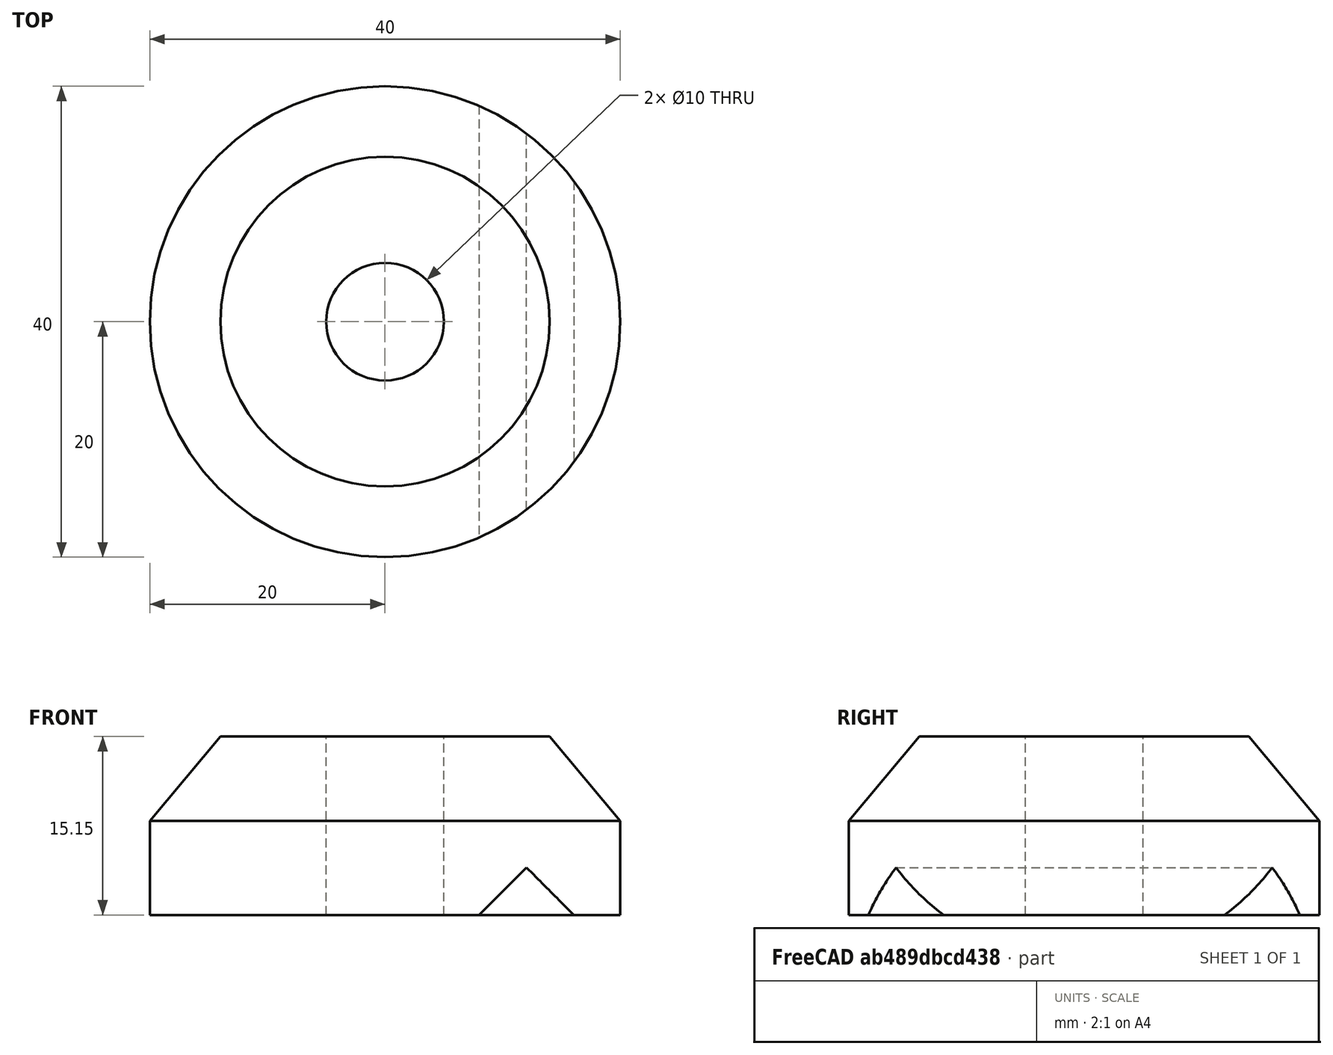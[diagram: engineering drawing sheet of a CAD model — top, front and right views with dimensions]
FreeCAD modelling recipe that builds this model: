
FCSTD DOCUMENT  (FreeCAD 0.19R)
Label: BBaligner
License: All rights reserved
LicenseURL: http://en.wikipedia.org/wiki/All_rights_reserved
objects: Sketcher::SketchObject×1, PartDesign::Revolution×1, PartDesign::Body×1, Part::Box×1, Part::Cut×1, Mesh::Feature×1
note: 6 computed .brp shape members not serialized (recipe doc carries the construction recipe); baked Part::Feature solids carry a one-line shape summary decoded from their .brp

FEATURE [Sketcher::SketchObject] Sketch
  FullyConstrained = true
  MapMode = 5
  Placement = pos=(0,0,0) rot=(1,0,0;1.5708rad)
  Support = -> [XZ_Plane]
  sketch-geometry (5):
    g0: LineSegment StartX=5 StartY=0 StartZ=0 EndX=5 EndY=15.1505 EndZ=0
    g1: LineSegment StartX=5 StartY=15.1505 StartZ=0 EndX=14 EndY=15.1505 EndZ=0
    g2: LineSegment StartX=14 StartY=15.1505 StartZ=0 EndX=20 EndY=8 EndZ=0
    g3: LineSegment StartX=20 StartY=8 StartZ=0 EndX=20 EndY=0 EndZ=0
    g4: LineSegment StartX=20 StartY=0 StartZ=0 EndX=5 EndY=0 EndZ=0
  constraints (15):
    c: PointOnObject(g0,g-1)
    c: Vertical(g0)
    c: Coincident(g0,g1)
    c: Horizontal(g1)
    c: Coincident(g1,g2)
    c: Coincident(g2,g3)
    c: PointOnObject(g3,g-1)
    c: Coincident(g3,g4)
    c: Coincident(g4,g0)
    c: Vertical(g3)
    c: Angle(g2) = -0.872665
    c: DistanceX(g0) = 5
    c: DistanceX(g1) = 14
    c: DistanceX(g2) = 20
    c: Distance(g3) = 8
FEATURE [PartDesign::Revolution] Revolution
  Angle = 360
  Axis = (0,2e-16,1)
  Base = (0,0,0)
  Placement = pos=(0,0,0) rot=(1,0,0;1.5708rad)
  Profile = -> Sketch
  ReferenceAxis = -> Sketch [V_Axis]
  Reversed = true
FEATURE [PartDesign::Body] Body
  Group = -> [Sketch,Revolution]
  Origin = -> Origin
  Tip = -> Revolution
FEATURE [Part::Box] Box  label="Cube"
  AttacherType = Attacher::AttachEngine3D
  Height = 17
  Length = 28
  Placement = pos=(0,-20,-8) rot=(0,1,0;0.785398rad)
  Width = 50
FEATURE [Part::Cut] Cut
  Base = -> Revolution
  Tool = -> Box
FEATURE [Mesh::Feature] Mesh  label="Cut (Meshed)"
